# Revit family: 94754 221  Cooktop Duo 4EI 80  Depuração
name_source: partatom
category: Modelos genéricos
units: mm (PartAtom-declared; Revit-internal decimal feet)

## family parameters
Com base no plano de trabalho = Não
Compartilhado = Não
Corte com vazios quando carregada = Não
Cota do conector redondo = Utilizar diâmetro
Pode hospedar o vergalhão = Não
Ponto de cálculo do ambiente = Não
Sempre na vertical = Sim
Tipo de parte = Normal

## types (1)
- 94754 221  Cooktop Duo 4EI 80  Depuração
    Coifa - Filtro Metálico = 2 filtros metálicos para gordura
    Coifa - Filtro de carvão = 1 filtro de carvão ativado Ambifresh retangular 5 DUO
    Coifa - Modo Automático = A velocidade da coifa se ajusta de acordo com a potência utilizada no cooktop
    Coifa - Nível de ruído = 63 db(A) - cfe. Norma IEC 60704
    Coifa - Potência máxima (kW) = 135 W
    Coifa - Reservatório = 2 reservatórios para líquidos. Em caso dederramamento de líquido na coifa, faça a remoção através dos reservatórios.
Acompanha tubululação para escoamento dos vapores do cozimento
    Coifa - Vazão = 600 m3/hora - cfe. Norma IEC 61591
    Coifa - Velocidades = 5 velocidades + Booster5 velocidades + Booster
    Cooktop - Bloqueio do Painel = Sim
    Cooktop - Função Pause = permite pausar e retomar o cozimento
    Cooktop - Função manter aquecido = mantém a comida na temperatura ideal para servir
    Cooktop - Potência Máxima (kW) = 7,20 kW
    Cooktop - Áreas de aquecimento = 4 áreas de aquecimento + Booster e função bridge
    Descrição = Cooktop de indução
    Dimensões = 770 x 520 mm
    Diâmetro máximo da panela (mm) = Ø 220 mm
    Diâmetro mínimo da panela (mm) = Ø 140 mm
    Elevação padrão = 0 mm  [stored 0 ft]
    Espessura = 1 mm
    Fabricante = Tramontina
    Frequência = 50-60 hz
    Funcionamento = Elétrico por Indução
    Instalação = Flush ou Semi-Flush
    Material predominante = Vitrocerâmico preto
    Modelo = Cooktop de indução DUO 4EI 80
    Painel de comando = Touch
    Panelas = Com fundo em material ferroso (que atrai ímã), com exceção para panelas em ferro fundido, estas não devem ser utilizadas.
    Referência do produto = 94754/221
    Superfície = Vitrocerâmica
    Tensão = 220 V
    Tipo = Cooktop com coifa integrado
    URL do fabricante = tramontina.com.br
    Uso exclusivo = Doméstico

note: [stored X ft] marks values corroborated as IEEE doubles in the binary element streams (Revit-internal decimal feet)
